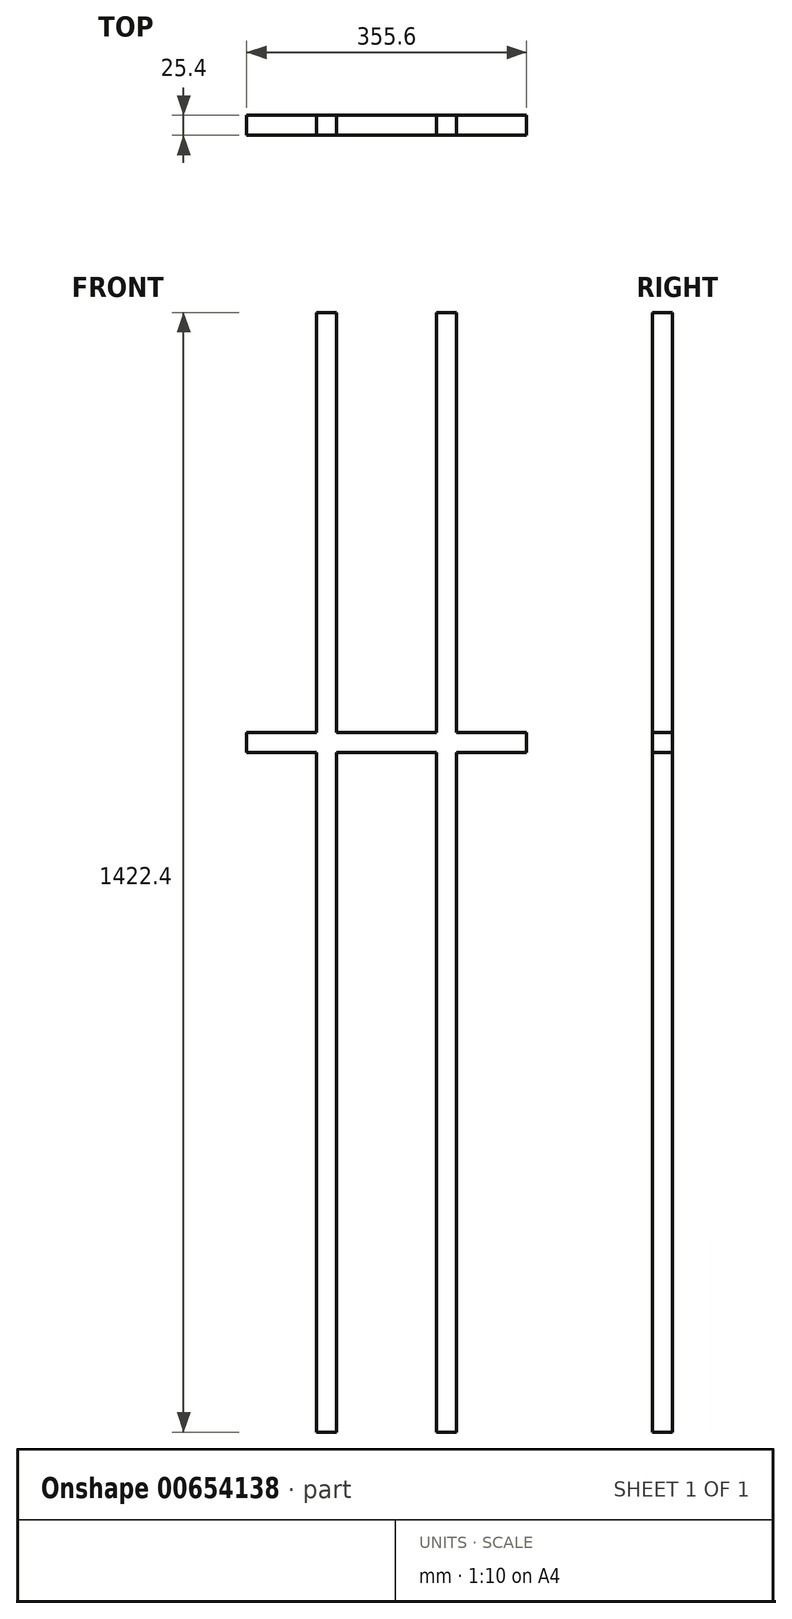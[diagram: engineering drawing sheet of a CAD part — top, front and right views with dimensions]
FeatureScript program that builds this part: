
annotation { "Feature Type Name" : "Feature", "Feature Type Description" : "" }
export const myFeature = defineFeature(function(context is Context, id is Id, definition is map)
    precondition{}
    {
        {
            var Q0;
            Q0=qCreatedBy(makeId("Front.planeOp"),FACE);
            var sketch = newSketch(context, id + "F0", { "sketchPlane" : qUnion([Q0])});
            skLineSegment(sketch, "E0", {"start": v(-88.9, 546.1) * mm, "end": v(-63.5, 546.1) * mm});
            skLineSegment(sketch, "E1", {"start": v(-63.5, 546.1) * mm, "end": v(-63.5, 12.7) * mm});
            skLineSegment(sketch, "E2", {"start": v(-63.5, 12.7) * mm, "end": v(63.5, 12.7) * mm});
            skLineSegment(sketch, "E3", {"start": v(63.5, 12.7) * mm, "end": v(63.5, 546.1) * mm});
            skLineSegment(sketch, "E4", {"start": v(63.5, 546.1) * mm, "end": v(88.9, 546.1) * mm});
            skLineSegment(sketch, "E5", {"start": v(88.9, 546.1) * mm, "end": v(88.9, 12.7) * mm});
            skLineSegment(sketch, "E6", {"start": v(88.9, 12.7) * mm, "end": v(177.8, 12.7) * mm});
            skLineSegment(sketch, "E7", {"start": v(177.8, 12.7) * mm, "end": v(177.8, -12.7) * mm});
            skLineSegment(sketch, "E8", {"start": v(177.8, -12.7) * mm, "end": v(88.9, -12.7) * mm});
            skLineSegment(sketch, "E9", {"start": v(88.9, -12.7) * mm, "end": v(88.9, -876.3) * mm});
            skLineSegment(sketch, "E10", {"start": v(88.9, -876.3) * mm, "end": v(63.5, -876.3) * mm});
            skLineSegment(sketch, "E11", {"start": v(63.5, -876.3) * mm, "end": v(63.5, -12.7) * mm});
            skLineSegment(sketch, "E12", {"start": v(63.5, -12.7) * mm, "end": v(-63.5, -12.7) * mm});
            skLineSegment(sketch, "E13", {"start": v(-63.5, -12.7) * mm, "end": v(-63.5, -876.3) * mm});
            skLineSegment(sketch, "E14", {"start": v(-63.5, -876.3) * mm, "end": v(-88.9, -876.3) * mm});
            skLineSegment(sketch, "E15", {"start": v(-88.9, -876.3) * mm, "end": v(-88.9, -12.7) * mm});
            skLineSegment(sketch, "E16", {"start": v(-88.9, -12.7) * mm, "end": v(-177.8, -12.7) * mm});
            skLineSegment(sketch, "E17", {"start": v(-177.8, -12.7) * mm, "end": v(-177.8, 12.7) * mm});
            skLineSegment(sketch, "E18", {"start": v(-177.8, 12.7) * mm, "end": v(-88.9, 12.7) * mm});
            skLineSegment(sketch, "E19", {"start": v(-88.9, 12.7) * mm, "end": v(-88.9, 546.1) * mm});
            skPoint(sketch, "E20", {"position": v(0, 0) * mm});
            skSolve(sketch);
        }
        {
            var Q0;
            Q0=qSketchRegion(id+"F0",true);
            extrude(context, id + "F1", {"entities" : qUnion([Q0]), "oppositeDirection" : true, "depth" : 25.4 * mm, "offsetDistance" : 25.4 * mm});
        }
    });
